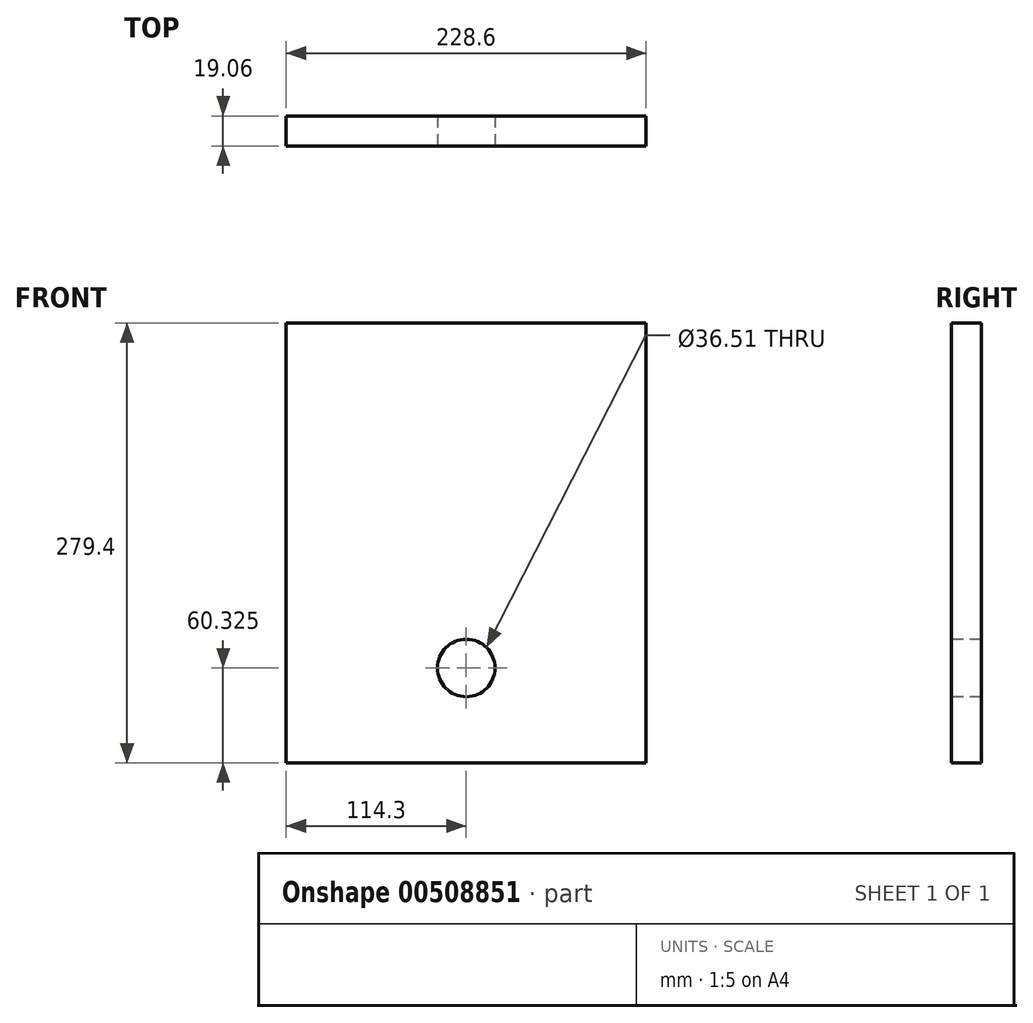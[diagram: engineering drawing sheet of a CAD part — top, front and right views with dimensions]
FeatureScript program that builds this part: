
annotation { "Feature Type Name" : "Feature", "Feature Type Description" : "" }
export const myFeature = defineFeature(function(context is Context, id is Id, definition is map)
    precondition{}
    {
        {
            var Q0;
            Q0=qCreatedBy(makeId("Front.planeOp"),FACE);
            var sketch = newSketch(context, id + "F0", { "sketchPlane" : qUnion([Q0])});
            skLineSegment(sketch, "E0.bottom", {"start": v(114.3, 139.7) * mm, "end": v(-114.3, 139.7) * mm});
            skLineSegment(sketch, "E0.top", {"start": v(114.3, -139.7) * mm, "end": v(-114.3, -139.7) * mm});
            skLineSegment(sketch, "E0.left", {"start": v(114.3, 139.7) * mm, "end": v(114.3, -139.7) * mm});
            skLineSegment(sketch, "E0.right", {"start": v(-114.3, 139.7) * mm, "end": v(-114.3, -139.7) * mm});
            skPoint(sketch, "E0.middle", {"position": v(0, 0) * mm});
            skSolve(sketch);
        }
        {
            var Q0;
            Q0=makeQuery(id+"F0.imprint","IMPRINT",FACE,{"disambiguationData":[TD([[makeQuery(id+"F0.imprint","IMPRINT",EDGE,{"derivedFrom":sQuery(id+"F0.wireOp",EDGE,"E0.bottom")}),1.0]])]});
            extrude(context, id + "F1", {"entities" : qUnion([Q0]), "endBound" : BoundingType.SYMMETRIC, "depth" : 19.05 * mm});
        }
        {
            var Q0;
            Q0=makeQuery(id+"F1.opExtrude","CAP_FACE",FACE,{"disambiguationData":[OSD([sQuery(id+"F0.wireOp",EDGE,"E0.bottom"),sQuery(id+"F0.wireOp",EDGE,"E0.top"),sQuery(id+"F0.wireOp",EDGE,"E0.left"),sQuery(id+"F0.wireOp",EDGE,"E0.right")])],"isStart":false});
            var sketch = newSketch(context, id + "F2", { "sketchPlane" : qUnion([Q0])});
            skPoint(sketch, "E1", {"position": v(0, -79.38) * mm});
            skSolve(sketch);
        }
        {
            var Q0;
            Q0=sQuery(id+"F2.wireOp",VERTEX,"E1");
            var Q1;
            Q1=makeQuery(id+"F1.opExtrude","SWEPT_BODY",BODY,{"disambiguationData":[OSD([sQuery(id+"F0.wireOp",EDGE,"E0.bottom"),sQuery(id+"F0.wireOp",EDGE,"E0.top"),sQuery(id+"F0.wireOp",EDGE,"E0.left"),sQuery(id+"F0.wireOp",EDGE,"E0.right")])]});
            hole(context, id + "F3", {"style" : HoleStyle.SIMPLE, "endStyle" : HoleEndStyle.THROUGH, "standardTappedOrClearance" : lookupTablePath({ "standard" : "ANSI", "engagement" : "75%", "pitch" : "18 tpi", "size" : "1 1/2", "type" : "Tapped" }), "standardBlindInLast" : lookupTablePath({ "standard" : "ANSI", "engagement" : "75%", "pitch" : "18 tpi", "size" : "1 1/2", "type" : "Tapped" }), "holeDiameter" : 36.5 * mm, "showTappedDepth" : true, "isTappedThrough" : true, "tappedDepth" : 16.09 * mm, "tapClearance" : 3, "locations" : qUnion([Q0]), "scope" : qUnion([Q1]), "majorDiameter" : 38.1 * mm});
        }
    });
